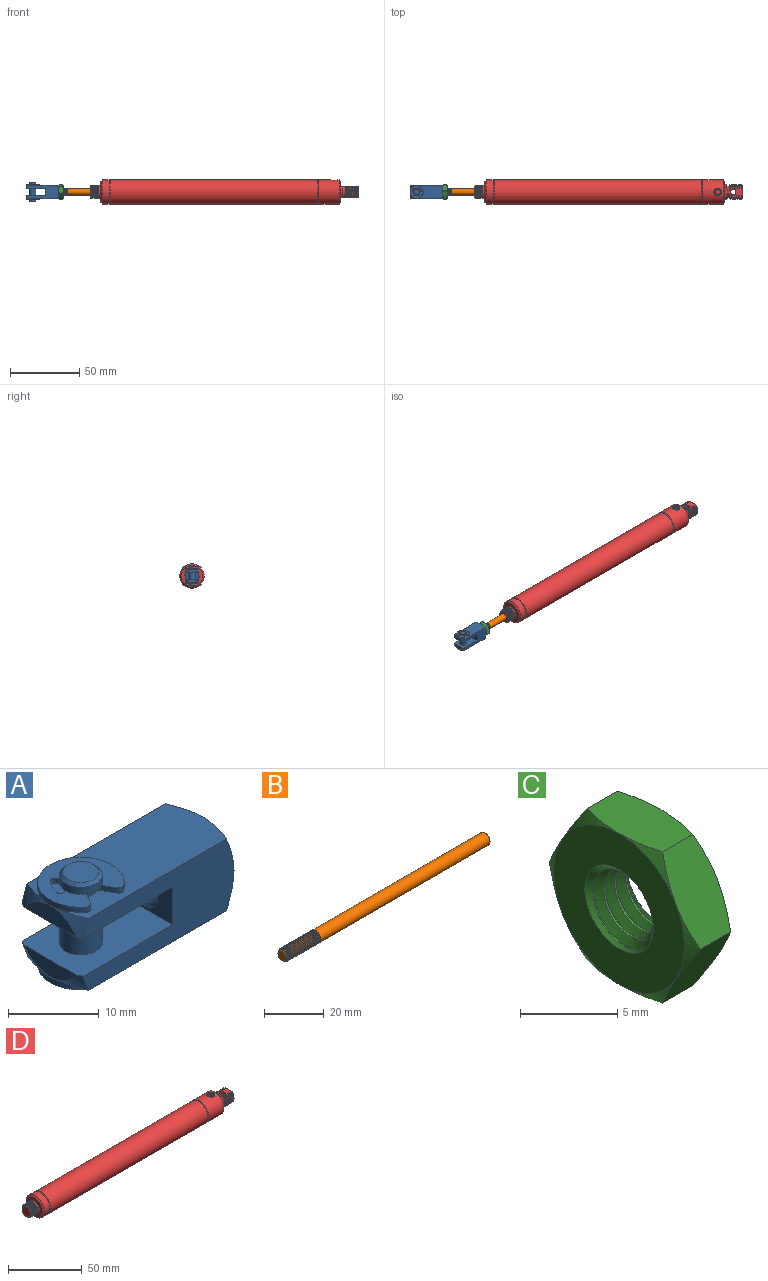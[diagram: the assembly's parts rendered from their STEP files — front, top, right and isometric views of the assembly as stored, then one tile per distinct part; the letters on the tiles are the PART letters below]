
ASSEMBLY  parts=4 mates=3
PART A: 76 faces, bbox 28.6x18.1x18.4 mm
  f0: cylinder r=1.88mm len=3.76mm, axis (0,0,-1), area 6.3mm2, adj f4,f5,f7,f11,f12,f17,f18,f24
  f1: cylinder r=2.37mm len=4.75mm, axis (0,0,-1), area 14.3mm2, adj f2,f4
  f2: cone r=2.37mm half-angle=45deg, axis (0,0,-1), area 7.4mm2, adj f1,f3
  f3: plane 3.99x3.99mm, normal (0,0,1), area 12.5mm2, adj f2
  f4: plane 4.75x4.75mm, normal (0,0,-1), area 6.6mm2, adj f0,f1
  f5: plane 28.24x14.04mm, normal (0,0,1), area 206.5mm2, adj f0,f34,f35,f37,f39
  f6: cylinder r=4.76mm len=9.53mm, axis (0,0,-1), area 16.5mm2, adj f9,f26,f27,f28
  f7: cylinder r=0.35mm len=0.7mm, axis (0,0,-1), area 0.3mm2, adj f0,f25,f27,f28
  f8: cylinder r=0.4mm len=0.7mm, axis (0,0,-1), area 0.5mm2, adj f13,f14,f27,f28
  f9: cylinder r=0.6mm len=0.88mm, axis (0,0,-1), area 0.7mm2, adj f6,f10,f27,f28
  f10: plane 1.66x0.96mm, normal (0.87,-0.5,0), area 1.3mm2, adj f9,f11,f27,f28
  f11: cylinder r=0.35mm len=0.7mm, axis (0,0,-1), area 0.3mm2, adj f0,f10,f27,f28
  f12: cylinder r=0.35mm len=0.7mm, axis (0,0,-1), area 0.3mm2, adj f0,f13,f27,f28
  f13: plane 0.7x0.69mm, normal (0,1,0), area 0.5mm2, adj f8,f12,f27,f28
  f14: cylinder r=3.32mm len=2.18mm, axis (0,0,-1), area 1.8mm2, adj f8,f15,f27,f28
  f15: cylinder r=0.4mm len=0.7mm, axis (0,0,-1), area 0.5mm2, adj f14,f16,f27,f28
  f16: plane 0.7x0.6mm, normal (-0.87,-0.5,0), area 0.5mm2, adj f15,f17,f27,f28
  f17: cylinder r=0.35mm len=0.7mm, axis (0,0,-1), area 0.3mm2, adj f0,f16,f27,f28
  f18: cylinder r=0.35mm len=0.7mm, axis (0,0,-1), area 0.3mm2, adj f0,f19,f27,f28
  f19: plane 0.7x0.6mm, normal (0.87,-0.5,0), area 0.5mm2, adj f18,f20,f27,f28
  f20: cylinder r=0.4mm len=0.7mm, axis (0,0,-1), area 0.5mm2, adj f19,f21,f27,f28
  f21: cylinder r=3.32mm len=2.18mm, axis (0,0,-1), area 1.8mm2, adj f20,f22,f27,f28
  f22: cylinder r=0.4mm len=0.7mm, axis (0,0,-1), area 0.5mm2, adj f21,f23,f27,f28
  f23: plane 0.7x0.69mm, normal (0,1,0), area 0.5mm2, adj f22,f24,f27,f28
  f24: cylinder r=0.35mm len=0.7mm, axis (0,0,-1), area 0.3mm2, adj f0,f23,f27,f28
  f25: plane 1.66x0.96mm, normal (-0.87,-0.5,0), area 1.3mm2, adj f7,f26,f27,f28
  f26: cylinder r=0.6mm len=0.88mm, axis (0,0,-1), area 0.7mm2, adj f6,f25,f27,f28
  f27: plane 9.54x8.65mm, normal (0,0,1), area 42.1mm2, adj f0,f6,f7,f8,f9,f10,f11,f12
  f28: plane 9.54x8.65mm, normal (0,0,-1), area 42.1mm2, adj f0,f6,f7,f8,f9,f10,f11,f12
  f29: cone r=2.5mm half-angle=45deg, axis (1,0,0), area 6.9mm2, adj f30,f31,f43,f44,f45
  f30: cylinder r=1.92mm len=8.94mm, axis (1,0,0), area 16.5mm2, adj f29,f32,f44,f45
  f31: plane 9.53x9.53mm, normal (1,0,0), area 51.6mm2, adj f29,f36,f37
  f32: plane 9.8x5.35mm, normal (-1,0,0), area 33.7mm2, adj f30,f34,f35,f41,f42,f43,f44,f45
  f33: plane 8.06x2.22mm, normal (-1,0,0), area 12.6mm2, adj f38,f41
  f34: plane 24.74x10.96mm, normal (0,-1,0), area 149.9mm2, adj f5,f32,f36,f37,f38,f39,f41,f42
  f35: plane 24.74x10.96mm, normal (0,1,0), area 149.8mm2, adj f5,f32,f36,f37,f38,f39,f41,f42
  f36: cone r=4.76mm half-angle=60deg, axis (-1,0,0), area 31mm2, adj f31,f34,f35,f52
  f37: cone r=4.76mm half-angle=60deg, axis (-1,0,0), area 31mm2, adj f5,f31,f34,f35
  f38: cone r=4.76mm half-angle=60deg, axis (1,0,0), area 11mm2, adj f33,f34,f35,f41,f52
  f39: cone r=4.76mm half-angle=60deg, axis (1,0,0), area 11mm2, adj f5,f34,f35,f40,f42
  f40: plane 8.06x2.22mm, normal (-1,0,0), area 12.6mm2, adj f39,f42
  f41: plane 14.3x9.55mm, normal (0,0,1), area 118mm2, adj f32,f33,f34,f35,f38,f46
  f42: plane 14.3x9.55mm, normal (0,0,-1), area 118mm2, adj f32,f34,f35,f39,f40,f46
  f43: bspline ~9.64x4.82mm, area 17.9mm2, adj f29,f32,f44,f45
  f44: bspline ~10.12x4.83mm, area 90.5mm2, adj f29,f30,f32,f43
  f45: bspline ~9.73x4.82mm, area 90.4mm2, adj f29,f30,f32,f43
  f46: cylinder r=2.37mm len=5.08mm, axis (0,0,-1), area 75.8mm2, adj f41,f42
  f47: plane 3.99x3.99mm, normal (0,0,-1), area 12.5mm2, adj f48
  f48: cone r=1.99mm half-angle=45deg, axis (0,0,1), area 7.4mm2, adj f47,f49
  f49: cylinder r=2.37mm len=4.75mm, axis (0,0,-1), area 14.3mm2, adj f48,f50
  f50: plane 4.75x4.75mm, normal (0,0,1), area 6.6mm2, adj f49,f51
  f51: cylinder r=1.88mm len=3.76mm, axis (0,0,-1), area 6.3mm2, adj f50,f52,f54,f58,f59,f64,f65,f71
  f52: plane 28.24x14.04mm, normal (0,0,-1), area 207.2mm2, adj f34,f35,f36,f38,f51
  f53: cylinder r=4.76mm len=9.53mm, axis (0,0,1), area 16.5mm2, adj f56,f73,f74,f75
  f54: cylinder r=0.35mm len=0.7mm, axis (0,0,1), area 0.3mm2, adj f51,f72,f74,f75
  f55: cylinder r=0.4mm len=0.7mm, axis (0,0,1), area 0.5mm2, adj f60,f61,f74,f75
  f56: cylinder r=0.6mm len=0.88mm, axis (0,0,1), area 0.7mm2, adj f53,f57,f74,f75
  f57: plane 1.66x0.96mm, normal (0.87,-0.5,0), area 1.3mm2, adj f56,f58,f74,f75
  f58: cylinder r=0.35mm len=0.7mm, axis (0,0,1), area 0.3mm2, adj f51,f57,f74,f75
  f59: cylinder r=0.35mm len=0.7mm, axis (0,0,1), area 0.3mm2, adj f51,f60,f74,f75
  f60: plane 0.7x0.69mm, normal (0,1,0), area 0.5mm2, adj f55,f59,f74,f75
  f61: cylinder r=3.32mm len=2.18mm, axis (0,0,1), area 1.8mm2, adj f55,f62,f74,f75
  f62: cylinder r=0.4mm len=0.7mm, axis (0,0,1), area 0.5mm2, adj f61,f63,f74,f75
  f63: plane 0.7x0.6mm, normal (-0.87,-0.5,0), area 0.5mm2, adj f62,f64,f74,f75
  f64: cylinder r=0.35mm len=0.7mm, axis (0,0,1), area 0.3mm2, adj f51,f63,f74,f75
  f65: cylinder r=0.35mm len=0.7mm, axis (0,0,1), area 0.3mm2, adj f51,f66,f74,f75
  f66: plane 0.7x0.6mm, normal (0.87,-0.5,0), area 0.5mm2, adj f65,f67,f74,f75
  f67: cylinder r=0.4mm len=0.7mm, axis (0,0,1), area 0.5mm2, adj f66,f68,f74,f75
  f68: cylinder r=3.32mm len=2.18mm, axis (0,0,1), area 1.8mm2, adj f67,f69,f74,f75
  f69: cylinder r=0.4mm len=0.7mm, axis (0,0,1), area 0.5mm2, adj f68,f70,f74,f75
  f70: plane 0.7x0.69mm, normal (0,1,0), area 0.5mm2, adj f69,f71,f74,f75
  f71: cylinder r=0.35mm len=0.7mm, axis (0,0,1), area 0.3mm2, adj f51,f70,f74,f75
  f72: plane 1.66x0.96mm, normal (-0.87,-0.5,0), area 1.3mm2, adj f54,f73,f74,f75
  f73: cylinder r=0.6mm len=0.88mm, axis (0,0,1), area 0.7mm2, adj f53,f72,f74,f75
  f74: plane 9.54x8.65mm, normal (0,0,-1), area 42.1mm2, adj f51,f53,f54,f55,f56,f57,f58,f59
  f75: plane 9.54x8.65mm, normal (0,0,1), area 42.1mm2, adj f51,f53,f54,f55,f56,f57,f58,f59
PART B: 27 faces, bbox 96.8x5.1x5.1 mm
  f0: cone r=1.82mm half-angle=45deg, axis (1,0,0), area 6.1mm2, adj f1,f21,f22,f23,f24
  f1: cylinder r=2.41mm len=4.83mm, axis (-1,0,0), area 0.8mm2, adj f0,f2,f22,f24
  f2: cylinder r=2.41mm len=4.83mm, axis (-1,0,0), area 0mm2, adj f1,f3,f22,f24
  f3: cylinder r=2.41mm len=4.83mm, axis (-1,0,0), area 1.5mm2, adj f2,f4,f22,f24
  f4: cylinder r=2.41mm len=4.83mm, axis (-1,0,0), area 1.5mm2, adj f3,f5,f22,f24
  f5: cylinder r=2.41mm len=4.83mm, axis (-1,0,0), area 1.5mm2, adj f4,f6,f22,f24
  f6: cylinder r=2.41mm len=4.83mm, axis (-1,0,0), area 1.5mm2, adj f5,f7,f22,f24
  f7: cylinder r=2.41mm len=4.83mm, axis (-1,0,0), area 1.5mm2, adj f6,f8,f22,f24
  f8: cylinder r=2.41mm len=4.83mm, axis (-1,0,0), area -6mm2, adj f7,f9,f22,f24
  f9: cylinder r=2.41mm len=4.83mm, axis (-1,0,0), area 1.5mm2, adj f8,f10,f22,f24
  f10: cylinder r=2.41mm len=4.83mm, axis (-1,0,0), area 1.5mm2, adj f9,f11,f22,f24
  f11: cylinder r=2.41mm len=4.83mm, axis (-1,0,0), area 1.5mm2, adj f10,f12,f22,f24
  f12: cylinder r=2.41mm len=4.83mm, axis (-1,0,0), area 1.5mm2, adj f11,f13,f22,f24
  f13: cylinder r=2.41mm len=4.83mm, axis (-1,0,0), area 1.5mm2, adj f12,f14,f22,f24
  f14: cylinder r=2.41mm len=4.83mm, axis (-1,0,0), area 1.5mm2, adj f13,f15,f22,f24
  f15: cylinder r=2.41mm len=4.83mm, axis (-1,0,0), area -6mm2, adj f14,f16,f22,f24
  f16: cylinder r=2.41mm len=4.83mm, axis (-1,0,0), area 1.5mm2, adj f15,f17,f22,f24
  f17: cylinder r=2.41mm len=4.83mm, axis (-1,0,0), area 1.5mm2, adj f16,f18,f22,f24
  f18: cylinder r=2.41mm len=4.83mm, axis (-1,0,0), area 1.5mm2, adj f17,f19,f22,f24
  f19: cylinder r=2.41mm len=4.83mm, axis (-1,0,0), area 1.5mm2, adj f18,f20,f22,f24
  f20: cylinder r=2.41mm len=80.86mm, axis (-1,0,0), area 1216.3mm2, adj f19,f22,f24,f25,f26
  f21: plane 3.64x3.64mm, normal (-1,0,0), area 10.4mm2, adj f0
  f22: bspline ~16.22x4.83mm, area -98.7mm2, adj f0,f1,f2,f3,f4,f5,f6,f7
  f23: bspline ~16.27x3.8mm, area 23.8mm2, adj f0,f22,f24,f25
  f24: bspline ~16.67x4.83mm, area 159.3mm2, adj f0,f1,f2,f3,f4,f5,f6,f7
  f25: plane 5.15x5.15mm, normal (-1,0,0), area 3.6mm2, adj f20,f22,f23,f24
  f26: plane 4.83x4.83mm, normal (1,0,0), area 18.3mm2, adj f20
PART C: 28 faces, bbox 4x11.5x11.5 mm
  f0: cone r=2.5mm half-angle=45deg, axis (1,0,0), area 6.8mm2, adj f1,f6,f13,f25,f26,f27
  f1: cone r=2.5mm half-angle=45deg, axis (1,0,0), area 0.1mm2, adj f0,f6,f27
  f2: cone r=2.5mm half-angle=45deg, axis (-1,0,0), area 6.2mm2, adj f3,f14,f25,f26,f27
  f3: cone r=2.5mm half-angle=45deg, axis (-1,0,0), area 0.8mm2, adj f2,f6,f26,f27
  f4: cone r=4.76mm half-angle=60deg, axis (-1,0,0), area 2.2mm2, adj f7,f8,f13
  f5: cone r=4.76mm half-angle=60deg, axis (1,0,0), area 2.2mm2, adj f10,f11,f14
  f6: cylinder r=1.92mm len=3.83mm, axis (-1,0,0), area 3.5mm2, adj f0,f1,f3,f26,f27
  f7: plane 5.21x3.5mm, normal (0,0.87,-0.5), area 15.2mm2, adj f4,f8,f12,f16,f19,f20
  f8: plane 5.21x3.5mm, normal (0,0.87,0.5), area 15.2mm2, adj f4,f7,f9,f18,f19,f24
  f9: plane 5.95x3.5mm, normal (0,0,1), area 15.2mm2, adj f8,f10,f17,f18,f23,f24
  f10: plane 5.21x3.5mm, normal (0,-0.87,0.5), area 15.2mm2, adj f5,f9,f11,f17,f22,f23
  f11: plane 5.21x3.5mm, normal (0,-0.87,-0.5), area 15.2mm2, adj f5,f10,f12,f15,f21,f22
  f12: plane 5.95x3.5mm, normal (0,0,-1), area 15.2mm2, adj f7,f11,f15,f16,f20,f21
  f13: plane 9.53x9.53mm, normal (1,0,0), area 51.6mm2, adj f0,f4,f20,f21,f22,f23,f24
  f14: plane 9.53x9.53mm, normal (-1,0,0), area 51.6mm2, adj f2,f5,f15,f16,f17,f18,f19
  f15: cone r=4.76mm half-angle=60deg, axis (1,0,0), area 2.2mm2, adj f11,f12,f14
  f16: cone r=4.76mm half-angle=60deg, axis (1,0,0), area 2.2mm2, adj f7,f12,f14
  f17: cone r=4.76mm half-angle=60deg, axis (1,0,0), area 2.2mm2, adj f9,f10,f14
  f18: cone r=4.76mm half-angle=60deg, axis (1,0,0), area 2.2mm2, adj f8,f9,f14
  f19: cone r=4.76mm half-angle=60deg, axis (1,0,0), area 2.2mm2, adj f7,f8,f14
  f20: cone r=4.76mm half-angle=60deg, axis (-1,0,0), area 2.2mm2, adj f7,f12,f13
  f21: cone r=4.76mm half-angle=60deg, axis (-1,0,0), area 2.2mm2, adj f11,f12,f13
  f22: cone r=4.76mm half-angle=60deg, axis (-1,0,0), area 2.2mm2, adj f10,f11,f13
  f23: cone r=4.76mm half-angle=60deg, axis (-1,0,0), area 2.2mm2, adj f9,f10,f13
  f24: cone r=4.76mm half-angle=60deg, axis (-1,0,0), area 2.2mm2, adj f8,f9,f13
  f25: bspline ~4.83x4.83mm, area 5.4mm2, adj f0,f2,f26,f27
  f26: bspline ~4.82x4.81mm, area 23.6mm2, adj f0,f2,f3,f6,f25
  f27: bspline ~4.83x4.83mm, area 23.6mm2, adj f0,f1,f2,f3,f6,f25
PART D: 112 faces, bbox 195.8x17.9x18.6 mm
  f0: torus R=5.18mm, axis (-1,0,0), area 33.5mm2, adj f40,f61,f63,f93,f95,f96
  f1: torus R=5.18mm, axis (-1,0,0), area 30.9mm2, adj f23,f36,f37,f62,f92,f95,f96
  f2: cone r=4.76mm half-angle=45deg, axis (1,0,0), area 23.9mm2, adj f9,f107,f108,f109,f110
  f3: cylinder r=4.76mm len=9.53mm, axis (1,0,0), area 46.3mm2, adj f4,f99,f107,f109,f111
  f4: cylinder r=4.76mm len=9.53mm, axis (1,0,0), area 4mm2, adj f3,f5,f107,f109
  f5: cylinder r=4.76mm len=9.53mm, axis (1,0,0), area 4mm2, adj f4,f6,f107,f109
  f6: cylinder r=4.76mm len=9.53mm, axis (1,0,0), area 4mm2, adj f5,f7,f107,f109
  f7: cylinder r=4.76mm len=9.53mm, axis (1,0,0), area 4mm2, adj f6,f8,f107,f109
  f8: cylinder r=4.76mm len=9.53mm, axis (1,0,0), area 4mm2, adj f7,f9,f107,f109
  f9: cylinder r=4.76mm len=3.37mm, axis (1,0,0), area 0.2mm2, adj f2,f8,f109
  f10: cylinder r=2.41mm len=4.83mm, axis (0,0,1), area 9.1mm2, adj f102,f103,f105,f106
  f11: cone r=2.65mm half-angle=15deg, axis (0,0,1), area 1.8mm2, adj f20,f102
  f12: cone r=8.76mm half-angle=45deg, axis (-1,0,0), area 74.5mm2, adj f20,f97
  f13: cone r=7.75mm half-angle=45deg, axis (1,0,0), area 74.5mm2, adj f16,f99
  f14: cone r=8.32mm half-angle=45deg, axis (1,0,0), area 33.3mm2, adj f20,f100
  f15: cone r=8.76mm half-angle=26.6deg, axis (-1,0,0), area 26.6mm2, adj f19,f100
  f16: cylinder r=8.76mm len=17.53mm, axis (-1,0,0), area 269.6mm2, adj f13,f17
  f17: cone r=8.76mm half-angle=45deg, axis (-1,0,0), area 33.3mm2, adj f16,f98
  f18: cone r=8.54mm half-angle=26.6deg, axis (1,0,0), area 26.6mm2, adj f19,f98
  f19: cylinder r=8.76mm len=150.25mm, axis (-1,0,0), area 8272.9mm2, adj f15,f18
  f20: cylinder r=8.76mm len=17.53mm, axis (-1,0,0), area 781.9mm2, adj f11,f12,f14,f101
  f21: cone r=2.41mm half-angle=45deg, axis (0,0,1), area 5.1mm2, adj f102,f103,f104,f105
  f22: cylinder r=1.99mm len=7.87mm, axis (0,0,1), area 98.6mm2, adj f95,f96
  f23: bspline ~5.56x5.56mm, area 0.2mm2, adj f1,f37,f96
  f24: cylinder r=5.56mm len=7.87mm, axis (1,0,0), area 1.4mm2, adj f32,f35,f95,f96
  f25: cylinder r=5.56mm len=7.87mm, axis (1,0,0), area 1.4mm2, adj f31,f34,f95,f96
  f26: cylinder r=5.56mm len=7.87mm, axis (1,0,0), area 1.4mm2, adj f30,f33,f95,f96
  f27: bspline ~9.46x4.73mm, area 1.5mm2, adj f33,f39,f95,f96
  f28: bspline ~9.46x4.73mm, area 1.5mm2, adj f30,f34,f95,f96
  f29: bspline ~9.46x4.73mm, area 1.5mm2, adj f31,f35,f95,f96
  f30: bspline ~11.11x5.56mm, area 8.6mm2, adj f26,f28,f95,f96
  f31: bspline ~11.11x5.56mm, area 8.6mm2, adj f25,f29,f95,f96
  f32: bspline ~11.11x5.56mm, area 8.6mm2, adj f24,f76,f95,f96
  f33: bspline ~11.11x5.56mm, area 8.6mm2, adj f26,f27,f95,f96
  f34: bspline ~11.11x5.56mm, area 8.6mm2, adj f25,f28,f95,f96
  f35: bspline ~11.11x5.56mm, area 8.6mm2, adj f24,f29,f95,f96
  f36: bspline ~11.11x5.56mm, area 8.2mm2, adj f1,f37,f64,f95,f96
  f37: bspline ~5.96x2.11mm, area 0.8mm2, adj f1,f23,f36,f96
  f38: cone r=4.76mm half-angle=45deg, axis (-1,0,0), area 5mm2, adj f74,f78,f95,f96
  f39: bspline ~11.11x5.56mm, area 8.4mm2, adj f27,f73,f75,f95,f96
  f40: plane 7.87x2.85mm, normal (1,0,0), area 4.4mm2, adj f0,f63,f94,f95,f96
  f41: cylinder r=5.56mm len=7.87mm, axis (1,0,0), area 13.3mm2, adj f92,f95,f96,f97
  f42: cylinder r=5.56mm len=3.94mm, axis (1,0,0), area 0.3mm2, adj f43,f44,f93,f95
  f43: bspline ~11.11x5.56mm, area 7.9mm2, adj f42,f67,f93,f95,f96
  f44: bspline ~0.01x0.01mm, area 0mm2, adj f42,f93,f95
  f45: cylinder r=5.56mm len=7.87mm, axis (1,0,0), area 1.4mm2, adj f55,f59,f95,f96
  f46: cylinder r=5.56mm len=7.87mm, axis (1,0,0), area 1.4mm2, adj f54,f58,f95,f96
  f47: cylinder r=5.56mm len=7.87mm, axis (1,0,0), area 1.4mm2, adj f53,f57,f95,f96
  f48: cone r=4.76mm half-angle=45deg, axis (-1,0,0), area 0.3mm2, adj f56,f74,f95
  f49: bspline ~9.46x4.73mm, area 1.5mm2, adj f57,f78,f95,f96
  f50: bspline ~9.46x4.73mm, area 1.5mm2, adj f53,f58,f95,f96
  f51: bspline ~9.46x4.73mm, area 1.5mm2, adj f54,f59,f95,f96
  f52: bspline ~9.46x4.73mm, area 1.5mm2, adj f55,f60,f95,f96
  f53: bspline ~11.11x5.56mm, area 8.6mm2, adj f47,f50,f95,f96
  f54: bspline ~11.11x5.56mm, area 8.6mm2, adj f46,f51,f95,f96
  f55: bspline ~11.11x5.56mm, area 8.6mm2, adj f45,f52,f95,f96
  f56: bspline ~9.49x5.56mm, area 0.4mm2, adj f48,f74,f77,f95
  f57: bspline ~11.11x5.56mm, area 8.6mm2, adj f47,f49,f95,f96
  f58: bspline ~11.11x5.56mm, area 8.6mm2, adj f46,f50,f95,f96
  f59: bspline ~11.11x5.56mm, area 8.6mm2, adj f45,f51,f95,f96
  f60: bspline ~11.11x5.56mm, area 8.6mm2, adj f52,f68,f95,f96
  f61: bspline ~1.14x1.07mm, area 0.1mm2, adj f0,f63,f96
  f62: bspline ~9.49x5.56mm, area 0.1mm2, adj f1,f92,f96
  f63: bspline ~9.49x5.56mm, area 0.3mm2, adj f0,f40,f61,f96
  f64: cylinder r=5.56mm len=7.87mm, axis (1,0,0), area 1.4mm2, adj f36,f65,f95,f96
  f65: bspline ~11.11x5.56mm, area 8.6mm2, adj f64,f91,f95,f96
  f66: bspline ~11.11x5.56mm, area 8.6mm2, adj f67,f72,f95,f96
  f67: bspline ~9.46x4.73mm, area 1.5mm2, adj f43,f66,f95,f96
  f68: cylinder r=5.56mm len=7.87mm, axis (1,0,0), area 1.4mm2, adj f60,f82,f95,f96
  f69: cylinder r=5.56mm len=7.87mm, axis (1,0,0), area 1.4mm2, adj f80,f85,f95,f96
  f70: cylinder r=5.56mm len=7.87mm, axis (1,0,0), area 1.4mm2, adj f83,f88,f95,f96
  f71: cylinder r=5.56mm len=7.87mm, axis (1,0,0), area 1.4mm2, adj f86,f90,f95,f96
  f72: cylinder r=5.56mm len=7.87mm, axis (1,0,0), area 1.4mm2, adj f66,f89,f95,f96
  f73: cylinder r=5.56mm len=3.94mm, axis (1,0,0), area 0.3mm2, adj f39,f75,f79,f95
  f74: plane 9.53x7.9mm, normal (1,0,0), area 65.1mm2, adj f38,f48,f56,f75,f77,f79,f95,f96
  f75: cone r=4.76mm half-angle=45deg, axis (-1,0,0), area 4.6mm2, adj f39,f73,f74,f79,f96
  f76: bspline ~9.46x4.73mm, area 1.5mm2, adj f32,f80,f95,f96
  f77: bspline ~7.28x2.11mm, area 1mm2, adj f56,f74,f79,f95
  f78: bspline ~11.11x5.56mm, area 4.5mm2, adj f38,f49,f95,f96
  f79: bspline ~8.9x2.93mm, area 4.5mm2, adj f73,f74,f75,f77,f95
  f80: bspline ~11.11x5.56mm, area 8.6mm2, adj f69,f76,f95,f96
  f81: bspline ~9.46x4.73mm, area 1.5mm2, adj f82,f83,f95,f96
  f82: bspline ~11.11x5.56mm, area 8.6mm2, adj f68,f81,f95,f96
  f83: bspline ~11.11x5.56mm, area 8.6mm2, adj f70,f81,f95,f96
  f84: bspline ~9.46x4.73mm, area 1.5mm2, adj f85,f86,f95,f96
  f85: bspline ~11.11x5.56mm, area 8.6mm2, adj f69,f84,f95,f96
  f86: bspline ~11.11x5.56mm, area 8.6mm2, adj f71,f84,f95,f96
  f87: bspline ~9.46x4.73mm, area 1.5mm2, adj f88,f89,f95,f96
  f88: bspline ~11.11x5.56mm, area 8.6mm2, adj f70,f87,f95,f96
  f89: bspline ~11.11x5.56mm, area 8.6mm2, adj f72,f87,f95,f96
  f90: bspline ~11.11x5.56mm, area 8.6mm2, adj f71,f91,f95,f96
  f91: bspline ~9.46x4.73mm, area 1.5mm2, adj f65,f90,f95,f96
  f92: plane 7.98x2.85mm, normal (1,0,0), area 4.1mm2, adj f1,f41,f62,f95,f96
  f93: plane 7.96x2.28mm, normal (-1,0,0), area 2.7mm2, adj f0,f42,f43,f44,f95,f96
  f94: cylinder r=5.56mm len=7.87mm, axis (1,0,0), area 13.3mm2, adj f40,f95,f96,f97
  f95: plane 12.94x8.08mm, normal (0,0,1), area 65mm2, adj f0,f1,f22,f24,f25,f26,f27,f28
  f96: plane 12.95x8.09mm, normal (0,0,-1), area 64.6mm2, adj f0,f1,f22,f23,f24,f25,f26,f27
  f97: plane 15.49x15.49mm, normal (1,0,0), area 109.1mm2, adj f12,f41,f94,f95,f96
  f98: plane 17.09x17.09mm, normal (-1,0,0), area 11.6mm2, adj f17,f18
  f99: plane 15.49x15.49mm, normal (-1,0,0), area 117.3mm2, adj f3,f13
  f100: plane 17.09x17.09mm, normal (1,0,0), area 11.6mm2, adj f14,f15
  f101: cone r=2.65mm half-angle=15deg, axis (0,0,1), area 0mm2, adj f20,f102
  f102: plane 5.31x5.31mm, normal (0,0,1), area 3.8mm2, adj f10,f11,f21,f101
  f103: bspline ~6.25x4.83mm, area 42.6mm2, adj f10,f21,f104,f106
  f104: bspline ~4.56x3.8mm, area 6.4mm2, adj f21,f103,f105,f106
  f105: bspline ~5.16x4.83mm, area 46.7mm2, adj f10,f21,f104,f106
  f106: plane 4.67x4.64mm, normal (0,0,1), area 14.7mm2, adj f10,f103,f104,f105
  f107: bspline ~9.53x9.53mm, area 122.7mm2, adj f2,f3,f4,f5,f6,f7,f8,f108
  f108: bspline ~8.15x8.15mm, area 19.9mm2, adj f2,f107,f109,f111
  f109: bspline ~9.53x9.53mm, area 133.7mm2, adj f2,f3,f4,f5,f6,f7,f8,f9
  f110: plane 7.94x7.94mm, normal (-1,0,0), area 49.5mm2, adj f2
  f111: plane 9.94x9.94mm, normal (-1,0,0), area 9.7mm2, adj f3,f107,f108,f109
PLACE A rot(axis=(-1,0,0),0deg) t=(-32.12,0,0)mm
PLACE B rot(axis=(1,0,0),180deg) t=(72.78,0,0)mm
PLACE C rot(axis=(-1,0,0),45deg) t=(-35.17,0,0)mm
PLACE D t=(89.03,0,0)mm
MATE slider B.f0 <-> D.f2  axis (-1,0,0) through (-16.25,0,0)mm
MATE fastened B.f0 <-> A.f29  axis (-1,0,0) through (-32.25,0,0)mm
MATE fastened C.f2 <-> A.f29  axis (-1,0,0) through (-22.6,0,0)mm
